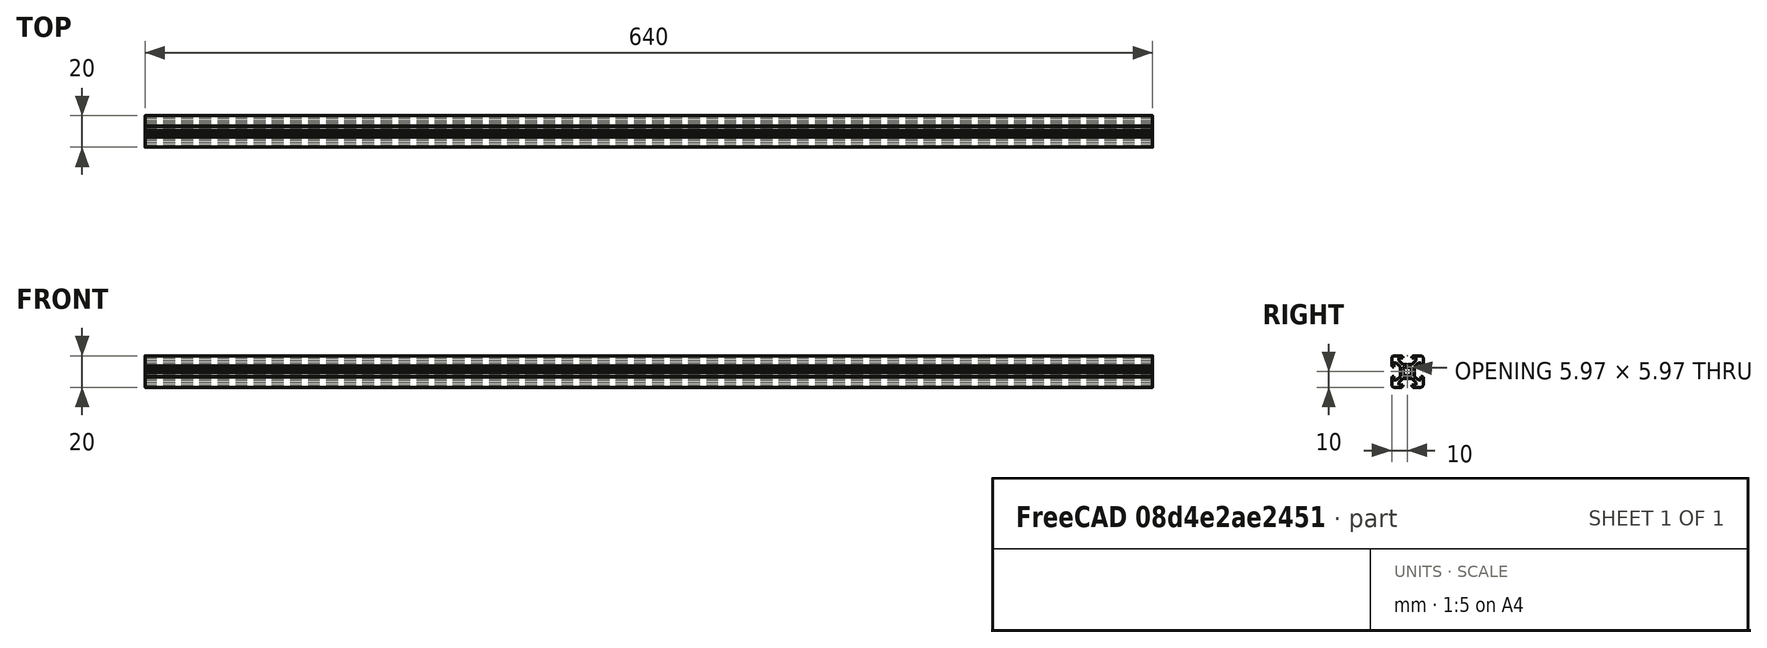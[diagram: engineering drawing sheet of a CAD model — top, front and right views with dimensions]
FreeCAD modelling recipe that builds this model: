
FCSTD DOCUMENT  (FreeCAD 0.19R)
Label: Tslot64
License: All rights reserved
LicenseURL: http://en.wikipedia.org/wiki/All_rights_reserved
objects: Sketcher::SketchObject×1, PartDesign::Pad×1, PartDesign::Body×1
note: 4 computed .brp shape members not serialized (recipe doc carries the construction recipe); baked Part::Feature solids carry a one-line shape summary decoded from their .brp

FEATURE [Sketcher::SketchObject] Sketch  label="T-Slot-Skizze"
  FullyConstrained = true
  MapMode = 5
  Placement = pos=(0,0,0) rot=(0.57735,0.57735,0.57735;2.0944rad)
  Support = -> [YZ_Plane]
  sketch-geometry (98):
    g0: LineSegment StartX=0 StartY=4.1 StartZ=0 EndX=0.65 EndY=4.5 EndZ=0
    g1: LineSegment StartX=0.65 StartY=4.5 StartZ=0 EndX=3 EndY=4.5 EndZ=0
    g2: LineSegment StartX=3 StartY=4.5 StartZ=0 EndX=5.5 EndY=7 EndZ=0
    g3: LineSegment StartX=5.5 StartY=7 StartZ=0 EndX=5.5 EndY=8.5 EndZ=0
    g4: LineSegment StartX=5.5 StartY=8.5 StartZ=0 EndX=3 EndY=8.5 EndZ=0
    g5: LineSegment StartX=3 StartY=8.5 StartZ=0 EndX=3 EndY=9.5 EndZ=0
    g6: LineSegment StartX=3 StartY=9.5 StartZ=0 EndX=3.5 EndY=9.5 EndZ=0
    g7: LineSegment StartX=3.5 StartY=9.5 StartZ=0 EndX=3.5 EndY=10 EndZ=0
    g8: LineSegment StartX=3.5 StartY=10 StartZ=0 EndX=8.5 EndY=10 EndZ=0
    g9: LineSegment StartX=10 StartY=8.5 StartZ=0 EndX=10 EndY=3.5 EndZ=0
    g10: LineSegment StartX=10 StartY=3.5 StartZ=0 EndX=9.5 EndY=3.5 EndZ=0
    g11: LineSegment StartX=9.5 StartY=3.5 StartZ=0 EndX=9.5 EndY=3 EndZ=0
    g12: LineSegment StartX=9.5 StartY=3 StartZ=0 EndX=8.5 EndY=3 EndZ=0
    g13: LineSegment StartX=8.5 StartY=3 StartZ=0 EndX=8.5 EndY=5.5 EndZ=0
    g14: LineSegment StartX=8.5 StartY=5.5 StartZ=0 EndX=7 EndY=5.5 EndZ=0
    g15: LineSegment StartX=7 StartY=5.5 StartZ=0 EndX=4.5 EndY=3 EndZ=0
    g16: LineSegment StartX=4.5 StartY=3 StartZ=0 EndX=4.5 EndY=0.65 EndZ=0
    g17: LineSegment StartX=4.5 StartY=0.65 StartZ=0 EndX=4.1 EndY=0 EndZ=0
    g18: ArcOfCircle CenterX=8.5 CenterY=8.5 CenterZ=0 NormalX=0 NormalY=0 NormalZ=1 AngleXU=0 Radius=1.5 StartAngle=0 EndAngle=1.5708
    g19: LineSegment StartX=0 StartY=-4.1 StartZ=0 EndX=0.65 EndY=-4.5 EndZ=0
    g20: LineSegment StartX=0.65 StartY=-4.5 StartZ=0 EndX=3 EndY=-4.5 EndZ=0
    g21: LineSegment StartX=3 StartY=-4.5 StartZ=0 EndX=5.5 EndY=-7 EndZ=0
    g22: LineSegment StartX=5.5 StartY=-7 StartZ=0 EndX=5.5 EndY=-8.5 EndZ=0
    g23: LineSegment StartX=5.5 StartY=-8.5 StartZ=0 EndX=3 EndY=-8.5 EndZ=0
    g24: LineSegment StartX=3 StartY=-8.5 StartZ=0 EndX=3 EndY=-9.5 EndZ=0
    g25: LineSegment StartX=3 StartY=-9.5 StartZ=0 EndX=3.5 EndY=-9.5 EndZ=0
    g26: LineSegment StartX=3.5 StartY=-9.5 StartZ=0 EndX=3.5 EndY=-10 EndZ=0
    g27: LineSegment StartX=3.5 StartY=-10 StartZ=0 EndX=8.5 EndY=-10 EndZ=0
    g28: LineSegment StartX=10 StartY=-8.5 StartZ=0 EndX=10 EndY=-3.5 EndZ=0
    g29: LineSegment StartX=10 StartY=-3.5 StartZ=0 EndX=9.5 EndY=-3.5 EndZ=0
    g30: LineSegment StartX=9.5 StartY=-3.5 StartZ=0 EndX=9.5 EndY=-3 EndZ=0
    g31: LineSegment StartX=9.5 StartY=-3 StartZ=0 EndX=8.5 EndY=-3 EndZ=0
    g32: LineSegment StartX=8.5 StartY=-3 StartZ=0 EndX=8.5 EndY=-5.5 EndZ=0
    g33: LineSegment StartX=8.5 StartY=-5.5 StartZ=0 EndX=7 EndY=-5.5 EndZ=0
    g34: LineSegment StartX=7 StartY=-5.5 StartZ=0 EndX=4.5 EndY=-3 EndZ=0
    g35: LineSegment StartX=4.5 StartY=-3 StartZ=0 EndX=4.5 EndY=-0.65 EndZ=0
    g36: ArcOfCircle CenterX=8.5 CenterY=-8.5 CenterZ=0 NormalX=0 NormalY=0 NormalZ=1 AngleXU=0 Radius=1.5 StartAngle=4.71239 EndAngle=6.28319
    g37: LineSegment StartX=4.5 StartY=-0.65 StartZ=0 EndX=4.1 EndY=0 EndZ=0
    g38: LineSegment StartX=0 StartY=-4.1 StartZ=0 EndX=-0.65 EndY=-4.5 EndZ=0
    g39: LineSegment StartX=-0.65 StartY=-4.5 StartZ=0 EndX=-3 EndY=-4.5 EndZ=0
    g40: LineSegment StartX=-3 StartY=-4.5 StartZ=0 EndX=-5.5 EndY=-7 EndZ=0
    g41: LineSegment StartX=-5.5 StartY=-7 StartZ=0 EndX=-5.5 EndY=-8.5 EndZ=0
    g42: LineSegment StartX=-5.5 StartY=-8.5 StartZ=0 EndX=-3 EndY=-8.5 EndZ=0
    g43: LineSegment StartX=-3 StartY=-8.5 StartZ=0 EndX=-3 EndY=-9.5 EndZ=0
    g44: LineSegment StartX=-3 StartY=-9.5 StartZ=0 EndX=-3.5 EndY=-9.5 EndZ=0
    g45: LineSegment StartX=-3.5 StartY=-9.5 StartZ=0 EndX=-3.5 EndY=-10 EndZ=0
    g46: LineSegment StartX=-3.5 StartY=-10 StartZ=0 EndX=-8.5 EndY=-10 EndZ=0
    g47: LineSegment StartX=-10 StartY=-8.5 StartZ=0 EndX=-10 EndY=-3.5 EndZ=0
    g48: LineSegment StartX=-10 StartY=-3.5 StartZ=0 EndX=-9.5 EndY=-3.5 EndZ=0
    g49: LineSegment StartX=-9.5 StartY=-3.5 StartZ=0 EndX=-9.5 EndY=-3 EndZ=0
    g50: LineSegment StartX=-9.5 StartY=-3 StartZ=0 EndX=-8.5 EndY=-3 EndZ=0
    g51: LineSegment StartX=-8.5 StartY=-3 StartZ=0 EndX=-8.5 EndY=-5.5 EndZ=0
    g52: LineSegment StartX=-8.5 StartY=-5.5 StartZ=0 EndX=-7 EndY=-5.5 EndZ=0
    g53: LineSegment StartX=-7 StartY=-5.5 StartZ=0 EndX=-4.5 EndY=-3 EndZ=0
    g54: LineSegment StartX=-4.5 StartY=-3 StartZ=0 EndX=-4.5 EndY=-0.65 EndZ=0
    g55: ArcOfCircle CenterX=-8.5 CenterY=-8.5 CenterZ=0 NormalX=0 NormalY=0 NormalZ=1 AngleXU=0 Radius=1.5 StartAngle=3.14159 EndAngle=4.71239
    g56: LineSegment StartX=-4.5 StartY=-0.65 StartZ=0 EndX=-4.1 EndY=0 EndZ=0
    g57: LineSegment StartX=-0.65 StartY=4.5 StartZ=0 EndX=-3 EndY=4.5 EndZ=0
    g58: LineSegment StartX=-3 StartY=4.5 StartZ=0 EndX=-5.5 EndY=7 EndZ=0
    g59: LineSegment StartX=-5.5 StartY=7 StartZ=0 EndX=-5.5 EndY=8.5 EndZ=0
    g60: LineSegment StartX=-5.5 StartY=8.5 StartZ=0 EndX=-3 EndY=8.5 EndZ=0
    g61: LineSegment StartX=-3 StartY=8.5 StartZ=0 EndX=-3 EndY=9.5 EndZ=0
    g62: LineSegment StartX=-3 StartY=9.5 StartZ=0 EndX=-3.5 EndY=9.5 EndZ=0
    g63: LineSegment StartX=-3.5 StartY=9.5 StartZ=0 EndX=-3.5 EndY=10 EndZ=0
    g64: LineSegment StartX=-3.5 StartY=10 StartZ=0 EndX=-8.5 EndY=10 EndZ=0
    g65: LineSegment StartX=-10 StartY=8.5 StartZ=0 EndX=-10 EndY=3.5 EndZ=0
    g66: LineSegment StartX=-10 StartY=3.5 StartZ=0 EndX=-9.5 EndY=3.5 EndZ=0
    g67: LineSegment StartX=-9.5 StartY=3.5 StartZ=0 EndX=-9.5 EndY=3 EndZ=0
    g68: LineSegment StartX=-9.5 StartY=3 StartZ=0 EndX=-8.5 EndY=3 EndZ=0
    g69: LineSegment StartX=-8.5 StartY=3 StartZ=0 EndX=-8.5 EndY=5.5 EndZ=0
    g70: LineSegment StartX=-8.5 StartY=5.5 StartZ=0 EndX=-7 EndY=5.5 EndZ=0
    g71: LineSegment StartX=-7 StartY=5.5 StartZ=0 EndX=-4.5 EndY=3 EndZ=0
    g72: LineSegment StartX=-4.5 StartY=3 StartZ=0 EndX=-4.5 EndY=0.65 EndZ=0
    g73: ArcOfCircle CenterX=-8.5 CenterY=8.5 CenterZ=0 NormalX=0 NormalY=0 NormalZ=1 AngleXU=0 Radius=1.5 StartAngle=1.5708 EndAngle=3.14159
    g74: LineSegment StartX=-4.5 StartY=0.65 StartZ=0 EndX=-4.1 EndY=0 EndZ=0
    g75: LineSegment StartX=0 StartY=4.1 StartZ=0 EndX=-0.65 EndY=4.5 EndZ=0
    g76: Circle CenterX=0 CenterY=0 CenterZ=0 NormalX=0 NormalY=0 NormalZ=1 AngleXU=0 Radius=3.55
    g77: Circle CenterX=0 CenterY=0 CenterZ=0 NormalX=0 NormalY=0 NormalZ=1 AngleXU=0 Radius=2.75
    g78: LineSegment StartX=1.3405 StartY=2.40116 StartZ=0 EndX=1.92324 EndY=2.9839 EndZ=0
    g79: LineSegment StartX=1.92324 StartY=2.9839 StartZ=0 EndX=2.9839 EndY=1.92324 EndZ=0
    g80: LineSegment StartX=2.9839 StartY=1.92324 StartZ=0 EndX=2.40116 EndY=1.3405 EndZ=0
    g81: ArcOfCircle CenterX=0 CenterY=0 CenterZ=0 NormalX=0 NormalY=0 NormalZ=1 AngleXU=0 Radius=2.75 StartAngle=0 EndAngle=0.509172
    g82: ArcOfCircle CenterX=0 CenterY=0 CenterZ=0 NormalX=0 NormalY=0 NormalZ=1 AngleXU=0 Radius=2.75 StartAngle=1.06162 EndAngle=1.5708
    g83: LineSegment StartX=-1.3405 StartY=2.40116 StartZ=0 EndX=-1.92324 EndY=2.9839 EndZ=0
    g84: LineSegment StartX=-1.92324 StartY=2.9839 StartZ=0 EndX=-2.9839 EndY=1.92324 EndZ=0
    g85: LineSegment StartX=-2.9839 StartY=1.92324 StartZ=0 EndX=-2.40116 EndY=1.3405 EndZ=0
    g86: ArcOfCircle CenterX=-1.3e-15 CenterY=6e-16 CenterZ=0 NormalX=0 NormalY=0 NormalZ=1 AngleXU=0 Radius=2.75 StartAngle=2.63242 EndAngle=3.14159
    g87: ArcOfCircle CenterX=-1.3e-15 CenterY=6e-16 CenterZ=0 NormalX=0 NormalY=0 NormalZ=1 AngleXU=0 Radius=2.75 StartAngle=1.5708 EndAngle=2.07997
    g88: LineSegment StartX=-1.34051 StartY=-2.40115 StartZ=0 EndX=-1.92325 EndY=-2.98389 EndZ=0
    g89: LineSegment StartX=-1.92325 StartY=-2.98389 StartZ=0 EndX=-2.9839 EndY=-1.92323 EndZ=0
    g90: LineSegment StartX=-2.9839 StartY=-1.92323 StartZ=0 EndX=-2.40116 EndY=-1.34049 EndZ=0
    g91: ArcOfCircle CenterX=-3e-16 CenterY=2e-16 CenterZ=0 NormalX=0 NormalY=0 NormalZ=1 AngleXU=0 Radius=2.75 StartAngle=3.14159 EndAngle=3.65076
    g92: ArcOfCircle CenterX=-3e-16 CenterY=2e-16 CenterZ=0 NormalX=0 NormalY=0 NormalZ=1 AngleXU=0 Radius=2.75 StartAngle=4.20321 EndAngle=4.71239
    g93: LineSegment StartX=1.34051 StartY=-2.40115 StartZ=0 EndX=1.92325 EndY=-2.98389 EndZ=0
    g94: LineSegment StartX=1.92325 StartY=-2.98389 StartZ=0 EndX=2.9839 EndY=-1.92323 EndZ=0
    g95: LineSegment StartX=2.9839 StartY=-1.92323 StartZ=0 EndX=2.40116 EndY=-1.34049 EndZ=0
    g96: ArcOfCircle CenterX=3e-16 CenterY=2e-16 CenterZ=0 NormalX=0 NormalY=0 NormalZ=1 AngleXU=0 Radius=2.75 StartAngle=4.71239 EndAngle=5.22156
    g97: ArcOfCircle CenterX=3e-16 CenterY=2e-16 CenterZ=0 NormalX=0 NormalY=0 NormalZ=1 AngleXU=0 Radius=2.75 StartAngle=5.77402 EndAngle=6.28319
  constraints (291):
    c: PointOnObject(g0,g-2)
    c: Coincident(g0,g1)
    c: Horizontal(g1)
    c: Coincident(g1,g2)
    c: Coincident(g2,g3)
    c: Vertical(g3)
    c: Coincident(g3,g4)
    c: Horizontal(g4)
    c: Coincident(g4,g5)
    c: Vertical(g5)
    c: Coincident(g5,g6)
    c: Horizontal(g6)
    c: Coincident(g6,g7)
    c: Coincident(g7,g8)
    c: Horizontal(g8)
    c: Vertical(g7)
    c: DistanceX(g-1,g5) = 3
    c: DistanceY(g4,g7) = 1.5
    c: DistanceY(g0,g7) = 5.5
    c: DistanceY(g3,g3) = 1.5
    c: DistanceY(g4,g5) = 1
    c: DistanceX(g-1,g1) = 3
    c: DistanceX(g-1,g7) = 3.5
    c: DistanceX(g0,g0) = 0.65
    c: DistanceY(g0,g0) = 0.4
    c: DistanceX(g-1,g3) = 5.5
    c: Vertical(g9)
    c: Coincident(g9,g10)
    c: Coincident(g10,g11)
    c: Coincident(g11,g12)
    c: Coincident(g12,g13)
    c: Vertical(g13)
    c: Coincident(g13,g14)
    c: Horizontal(g14)
    c: Coincident(g14,g15)
    c: Coincident(g15,g16)
    c: Vertical(g16)
    c: Coincident(g16,g17)
    c: PointOnObject(g17,g-1)
    c: Horizontal(g10)
    c: Horizontal(g12)
    c: Vertical(g11)
    c: Equal(g17,g0)
    c: Equal(g1,g16)
    c: Equal(g15,g2)
    c: Equal(g3,g14)
    c: Equal(g13,g4)
    c: Equal(g12,g5)
    c: Parallel(g15,g2)
    c: Equal(g11,g6)
    c: Equal(g10,g7)
    c: Equal(g9,g8)
    c: Tangent(g8,g18) = 1.5708
    c: Tangent(g9,g18) = 1.5708
    c: Radius(g18) = 1.5
    c: DistanceY(g-1,g8) = 10
    c: DistanceX(g-1,g9) = 10
    c: Coincident(g19,g20)
    c: Horizontal(g20)
    c: Coincident(g20,g21)
    c: Coincident(g21,g22)
    c: Vertical(g22)
    c: Coincident(g22,g23)
    c: Horizontal(g23)
    c: Coincident(g23,g24)
    c: Vertical(g24)
    c: Coincident(g24,g25)
    c: Horizontal(g25)
    c: Coincident(g25,g26)
    c: Coincident(g26,g27)
    c: Horizontal(g27)
    c: Vertical(g26)
    c: Vertical(g28)
    c: Coincident(g28,g29)
    c: Coincident(g29,g30)
    c: Coincident(g30,g31)
    c: Coincident(g31,g32)
    c: Vertical(g32)
    c: Coincident(g32,g33)
    c: Horizontal(g33)
    c: Coincident(g33,g34)
    c: Coincident(g34,g35)
    c: Vertical(g35)
    c: Coincident(g35,g37)
    c: Horizontal(g29)
    c: Horizontal(g31)
    c: Vertical(g30)
    c: Equal(g37,g19)
    c: Equal(g20,g35)
    c: Equal(g34,g21)
    c: Equal(g22,g33)
    c: Equal(g32,g23)
    c: Equal(g31,g24)
    c: Parallel(g34,g21)
    c: Equal(g30,g25)
    c: Equal(g29,g26)
    c: Equal(g28,g27)
    c: Tangent(g27,g36) = -1.5708
    c: Tangent(g28,g36) = -1.5708
    c: Radius(g36) = 1.5
    c: Equal(g9,g28)
    c: Equal(g12,g31)
    c: DistanceX(g-1,g28) = 10
    c: DistanceY(g27,g-1) = 10
    c: DistanceY(g30,g-1) = 3
    c: Equal(g33,g14)
    c: Equal(g35,g16)
    c: Equal(g17,g37)
    c: Coincident(g37,g17)
    c: Equal(g15,g34)
    c: PointOnObject(g19,g-2)
    c: DistanceY(g34,g-1) = 3
    c: DistanceX(g-1,g20) = 3
    c: Coincident(g38,g39)
    c: Horizontal(g39)
    c: Coincident(g39,g40)
    c: Coincident(g40,g41)
    c: Vertical(g41)
    c: Coincident(g41,g42)
    c: Horizontal(g42)
    c: Coincident(g42,g43)
    c: Vertical(g43)
    c: Coincident(g43,g44)
    c: Horizontal(g44)
    c: Coincident(g44,g45)
    c: Coincident(g45,g46)
    c: Horizontal(g46)
    c: Vertical(g45)
    c: Vertical(g47)
    c: Coincident(g47,g48)
    c: Coincident(g48,g49)
    c: Coincident(g49,g50)
    c: Coincident(g50,g51)
    c: Vertical(g51)
    c: Coincident(g51,g52)
    c: Horizontal(g52)
    c: Coincident(g52,g53)
    c: Coincident(g53,g54)
    c: Vertical(g54)
    c: Coincident(g54,g56)
    c: Horizontal(g48)
    c: Horizontal(g50)
    c: Vertical(g49)
    c: Equal(g39,g54)
    c: Equal(g53,g40)
    c: Equal(g41,g52)
    c: Equal(g51,g42)
    c: Equal(g50,g43)
    c: Parallel(g53,g40)
    c: Equal(g49,g44)
    c: Equal(g48,g45)
    c: Equal(g47,g46)
    c: Tangent(g46,g55) = 1.5708
    c: Tangent(g47,g55) = 1.5708
    c: Radius(g55) = 1.5
    c: Coincident(g38,g19)
    c: DistanceX(g39,g-1) = 3
    c: DistanceX(g38,g19) = 0.65
    c: DistanceY(g38,g19) = 0.4
    c: PointOnObject(g56,g-1)
    c: Equal(g56,g38)
    c: DistanceY(g53,g-1) = 3
    c: Equal(g22,g41)
    c: Equal(g42,g23)
    c: Equal(g24,g43)
    c: Equal(g25,g44)
    c: Equal(g26,g45)
    c: DistanceY(g46,g-1) = 10
    c: DistanceX(g47,g-1) = 10
    c: Coincident(g75,g57)
    c: Horizontal(g57)
    c: Coincident(g57,g58)
    c: Coincident(g58,g59)
    c: Vertical(g59)
    c: Coincident(g59,g60)
    c: Horizontal(g60)
    c: Coincident(g60,g61)
    c: Vertical(g61)
    c: Coincident(g61,g62)
    c: Horizontal(g62)
    c: Coincident(g62,g63)
    c: Coincident(g63,g64)
    c: Horizontal(g64)
    c: Vertical(g63)
    c: Vertical(g65)
    c: Coincident(g65,g66)
    c: Coincident(g66,g67)
    c: Coincident(g67,g68)
    c: Coincident(g68,g69)
    c: Vertical(g69)
    c: Coincident(g69,g70)
    c: Horizontal(g70)
    c: Coincident(g70,g71)
    c: Coincident(g71,g72)
    c: Vertical(g72)
    c: Coincident(g72,g74)
    c: Horizontal(g66)
    c: Horizontal(g68)
    c: Vertical(g67)
    c: Equal(g57,g72)
    c: Equal(g71,g58)
    c: Equal(g59,g70)
    c: Equal(g69,g60)
    c: Equal(g68,g61)
    c: Parallel(g71,g58)
    c: Equal(g67,g62)
    c: Equal(g66,g63)
    c: Equal(g65,g64)
    c: Tangent(g64,g73) = -1.5708
    c: Tangent(g65,g73) = -1.5708
    c: Radius(g73) = 1.5
    c: Equal(g74,g75)
    c: Coincident(g56,g74)
    c: Coincident(g0,g75)
    c: Equal(g0,g75)
    c: Equal(g1,g57)
    c: Equal(g2,g58)
    c: Equal(g3,g59)
    c: Equal(g4,g60)
    c: Equal(g5,g61)
    c: Equal(g6,g62)
    c: Equal(g7,g63)
    c: Equal(g8,g64)
    c: DistanceX(g65,g-1) = 10
    c: Coincident(g76,g-1)
    c: Coincident(g77,g-1)
    c: Radius(g76) = 3.55
    c: Radius(g77) = 2.75
    c: PointOnObject(g78,g77)
    c: PointOnObject(g78,g76)
    c: Coincident(g78,g79)
    c: PointOnObject(g79,g76)
    c: Coincident(g79,g80)
    c: PointOnObject(g80,g77)
    c: Coincident(g81,g-1)
    c: Coincident(g81,g80)
    c: Coincident(g82,g81)
    c: Coincident(g82,g78)
    c: Parallel(g78,g80)
    c: Parallel(g78,g2)
    c: Distance(g79) = 1.5
    c: Distance(g78,g80) = 1.5
    c: PointOnObject(g82,g-2)
    c: PointOnObject(g81,g-1)
    c: Coincident(g83,g84)
    c: Coincident(g84,g85)
    c: Coincident(g86,g85)
    c: Coincident(g87,g86)
    c: Coincident(g87,g83)
    c: Parallel(g83,g85)
    c: Distance(g84) = 1.5
    c: Distance(g83,g85) = 1.5
    c: Coincident(g82,g87)
    c: PointOnObject(g86,g-1)
    c: PointOnObject(g83,g76)
    c: PointOnObject(g83,g77)
    c: PointOnObject(g85,g77)
    c: PointOnObject(g84,g76)
    c: PointOnObject(g86,g77)
    c: Parallel(g85,g71)
    c: Coincident(g88,g89)
    c: Coincident(g89,g90)
    c: Coincident(g91,g90)
    c: Coincident(g92,g91)
    c: Coincident(g92,g88)
    c: Parallel(g88,g90)
    c: Distance(g89) = 1.5
    c: Distance(g88,g90) = 1.5
    c: PointOnObject(g88,g77)
    c: PointOnObject(g90,g77)
    c: Coincident(g86,g91)
    c: PointOnObject(g89,g76)
    c: PointOnObject(g88,g76)
    c: PointOnObject(g92,g-2)
    c: PointOnObject(g92,g77)
    c: Parallel(g88,g40)
    c: Coincident(g93,g94)
    c: Coincident(g94,g95)
    c: Coincident(g97,g95)
    c: Coincident(g96,g97)
    c: Coincident(g96,g93)
    c: Parallel(g93,g95)
    c: Distance(g94) = 1.5
    c: Distance(g93,g95) = 1.5
    c: Coincident(g81,g97)
    c: Coincident(g92,g96)
    c: PointOnObject(g93,g77)
    c: PointOnObject(g95,g77)
    c: PointOnObject(g94,g76)
    c: PointOnObject(g93,g76)
    c: Parallel(g93,g21)
FEATURE [PartDesign::Pad] Pad  label="T-Slot-Element"
  Direction = (1,1,1)
  Length = 640
  Length2 = 100
  Placement = pos=(0,0,0) rot=(0.57735,0.57735,0.57735;2.0944rad)
  Profile = -> Sketch
  Type = 0
FEATURE [PartDesign::Body] Body  label="T-Slot-Profil 20x20"
  Group = -> [Sketch,Pad]
  Origin = -> Origin
  Tip = -> Pad
